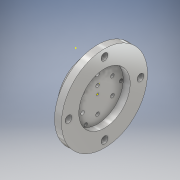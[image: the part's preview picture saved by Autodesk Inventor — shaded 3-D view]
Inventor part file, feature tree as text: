
AUTODESK INVENTOR PART (.ipt)
format: ipt  version: 2017.3 (Build 213256000, 256)  size: 292,864 bytes
history: native  units: mm
features: sketch x28, plane x23, extrude x12, hole x9, other x9, move_body x2
ambient origin geometry x8: Origin, YZ Plane, XZ Plane, XY Plane, X Axis, Y Axis, Z Axis, Center Point
bodies: Solid1 (feature_tree)
feature tree (83):
  extrude  "Extrusion1"  Depth=100.0mm TaperAngle=0.0deg
  sketch  "Sketch5"  dims[d13=-5.0mm d14=0.0mm d15=0.0mm d16=10.0mm d17=0.0mm d18=0.0mm]
  move_body  "Move Body1"
  move_body  "Move Body2"
  extrude  "Extrusion4"  Depth=10.0mm TaperAngle=0.0deg
  extrude  "Extrusion6"  Depth=5.0mm TaperAngle=0.0deg
  extrude  "Extrusion7"  Depth=95.0mm TaperAngle=0.0deg
  plane  "Work Plane4"
  plane  "Work Plane5"
  plane  "Work Plane11"
  extrude  "Extrusion8"  [1 undecoded]
  hole  "Hole8"  [1 undecoded]
  other  "Work Axis7"
  other  "Work Axis8"
  other  "Work Axis9"
  other  "Work Axis10"
  other  "Work Axis11"
  other  "Work Axis12"
  other  "Work Axis13"
  plane  "Work Plane27"
  plane  "Work Plane28"
  plane  "Work Plane29"
  plane  "Work Plane30"
  plane  "Work Plane31"
  plane  "Work Plane32"
  plane  "Work Plane33"
  plane  "Work Plane34"
  sketch  "Sketch27"  dims[d97=1.67mm d98=1.67mm]
  sketch  "Sketch28"  dims[d99=1.67mm d100=1.67mm]
  sketch  "Sketch29"  dims[d101=4.0mm d102=0.0mm]
  plane  "Work Plane35"
  plane  "Work Plane36"
  plane  "Work Plane37"
  plane  "Work Plane38"
  sketch  "Sketch30"  dims[d103=1.221mm d104=2.0mm d105=4.0mm d106=2.0mm d107=90.0deg d108=2.0mm d109=20.594885mm d110=-9.295mm d111=9.295mm d112=-9.295mm d113=9.295mm]
  sketch  "Sketch31"  dims[d114=9.295mm d115=-9.295mm]
  sketch  "Sketch32"  dims[d116=1.221mm d117=3.2mm d118=4.0mm d119=2.0mm d120=90.0deg d121=5.39mm d122=20.594885mm]
  sketch  "Sketch33"  dims[d123=1.221mm d124=3.2mm d125=4.0mm d126=2.0mm d127=90.0deg d128=5.39mm d129=20.594885mm]
  hole  "Hole9"  [1 undecoded]
  hole  "Hole10"  [1 undecoded]
  hole  "Hole12"  [1 undecoded]
  hole  "Hole13"  [1 undecoded]
  hole  "Hole14"  [1 undecoded]
  plane  "Work Plane42"
  plane  "Work Plane43"
  plane  "Work Plane44"
  sketch  "Sketch35"  dims[d137=1.221mm d138=3.2mm d139=4.0mm d140=2.0mm d141=90.0deg d142=5.39mm d143=20.594885mm]
  sketch  "Sketch39"  dims[d144=1.221mm d145=3.2mm d146=4.0mm d147=2.0mm d148=90.0deg d149=5.39mm d150=20.594885mm]
  extrude  "Extrusion9"  Depth=4.0mm TaperAngle=0.0deg
  hole  "Hole20"  [1 undecoded]
  extrude  "Extrusion11"  Depth=5.0mm TaperAngle=0.0deg
  extrude  "Extrusion12"  Depth=4.0mm TaperAngle=0.0deg
  extrude  "Extrusion13"  Depth=17.25mm
  extrude  "Extrusion14"  Depth=23.4mm
  sketch  "Sketch49"  dims[d222=95.0mm d223=0.0mm d224=17.25mm d225=-0.145mm]
  plane  "Work Plane46"
  sketch  "Sketch50"  dims[d226=1.221mm d227=3.2mm d228=4.0mm d229=2.0mm d230=90.0deg d231=5.3mm d232=20.594885mm d233=23.4mm]
  sketch  "Sketch51"  dims[d234=39.1mm d235=3.175mm d236=0.0mm]
  other  "Work Point1"
  hole  "Hole21"  [1 undecoded]
  extrude  "Extrusion15"  Depth=3.175mm
  extrude  "Extrusion16"  Depth=3.175mm
  hole  "Hole22"  [1 undecoded]
  sketch  "Sketch1"  dims[d0=26.4mm d1=100.0mm d2=0.0mm]
  sketch  "Sketch6"  dims[d21=1.0mm d22=5.0mm d23=0.0mm]
  sketch  "Sketch8"  dims[d35=22.0mm d36=95.0mm d37=0.0mm]
  sketch  "Sketch25"  dims[d38=90.0mm d39=0.0mm d47=-13.2mm]
  sketch  "Sketch26"  dims[d55=0.0mm d96=1.67mm]
  other  "Work Axis14"
  plane  "Work Plane39"
  plane  "Work Plane40"
  plane  "Work Plane41"
  sketch  "Sketch40"  dims[d151=1.221mm d152=3.2mm d153=4.0mm d154=2.0mm d155=90.0deg d156=5.39mm d157=20.594885mm d158=-2.617994mm]
  sketch  "Sketch44"  dims[d159=1.1mm d160=-26.4mm d161=90.0deg d162=13.2mm d163=-13.2mm]
  sketch  "Sketch45"  dims[d192=1.6mm d193=4.0mm d194=0.0mm]
  sketch  "Sketch46"  dims[d206=1.567mm d207=4.0mm d208=4.0mm d209=2.0mm d210=90.0deg d211=2.0mm d212=20.594885mm d213=1.6mm]
  sketch  "Sketch47"  dims[d214=5.0mm d215=0.0mm d217=4.0mm d218=0.0mm]
  sketch  "Sketch48"  dims[d219=1.67mm d220=4.0mm d221=0.0mm]
  plane  "Work Plane45"
  sketch  "Sketch52"  dims[d237=3.175mm d238=3.175mm]
  sketch  "Sketch53"  dims[d239=3.175mm d240=3.175mm]
  sketch  "Sketch54"  dims[d241=3.175mm d242=0.0mm]
  sketch  "Sketch55"  dims[d243=1.567mm d244=6.3mm d245=4.0mm d246=2.0mm d247=90.0deg d248=6.3mm d249=20.594885mm d199=1.0mm d200=1.0mm]
note: 10 required parameter values undecoded (feature->parameter linkage not recoverable at this tier; creation-order binding heuristic only, values carry confidence <= 0.55)
